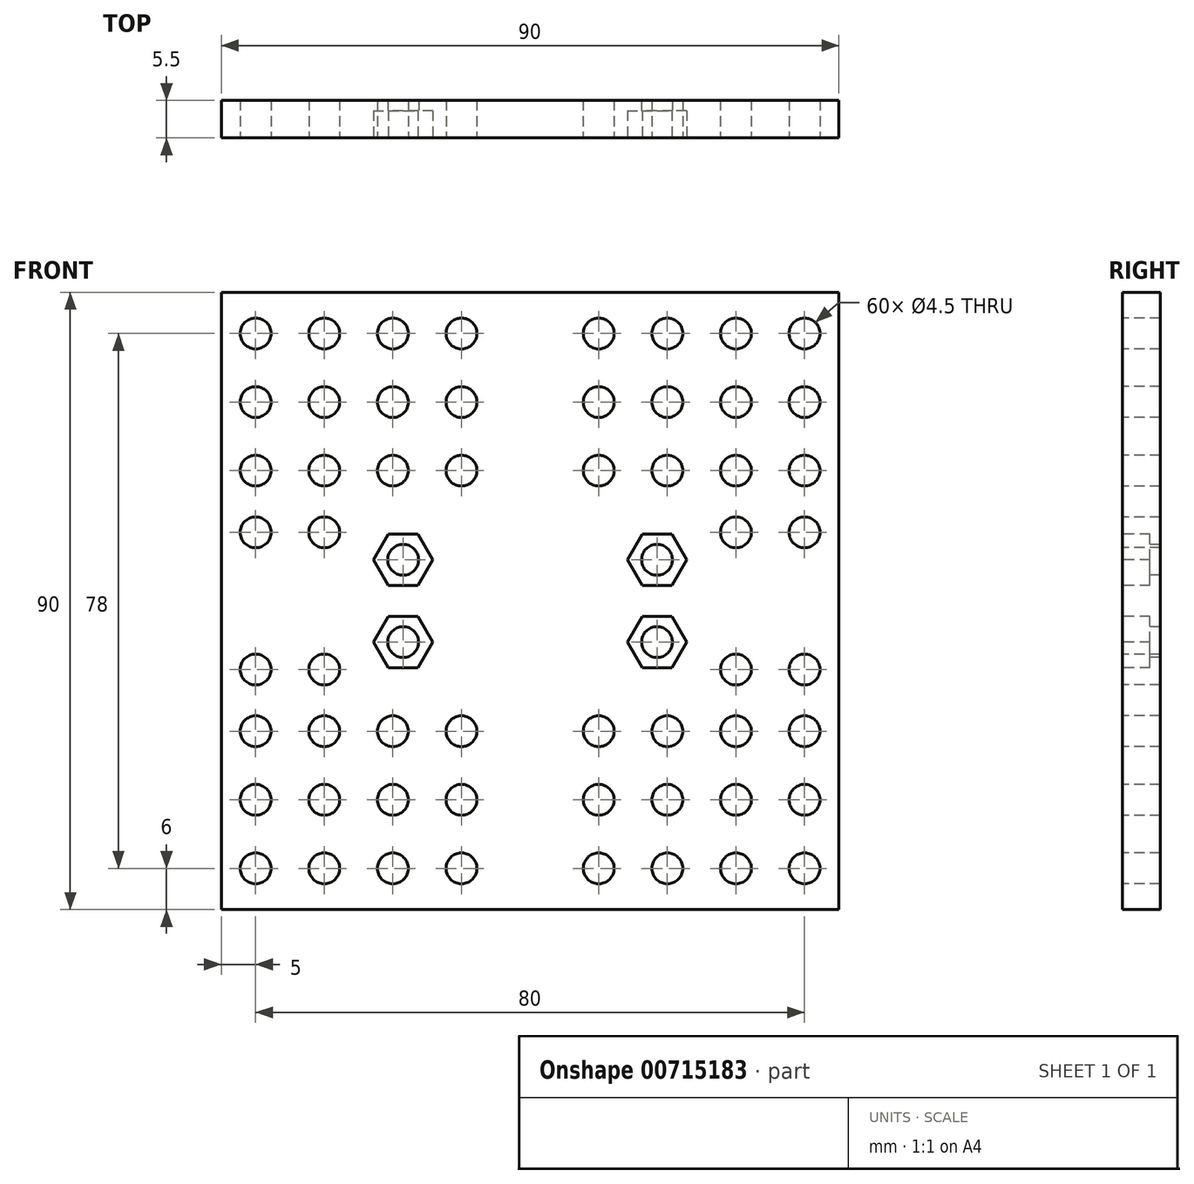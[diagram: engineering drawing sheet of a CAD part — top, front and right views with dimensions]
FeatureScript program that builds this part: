
annotation { "Feature Type Name" : "Feature", "Feature Type Description" : "" }
export const myFeature = defineFeature(function(context is Context, id is Id, definition is map)
    precondition{}
    {
        {
            var Q0;
            Q0=qCreatedBy(makeId("Front.planeOp"),FACE);
            var sketch = newSketch(context, id + "F0", { "sketchPlane" : qUnion([Q0])});
            skLineSegment(sketch, "E0.bottom", {"start": v(45, 45) * mm, "end": v(-45, 45) * mm});
            skLineSegment(sketch, "E0.top", {"start": v(45, -45) * mm, "end": v(-45, -45) * mm});
            skLineSegment(sketch, "E0.left", {"start": v(45, 45) * mm, "end": v(45, -45) * mm});
            skLineSegment(sketch, "E0.right", {"start": v(-45, 45) * mm, "end": v(-45, -45) * mm});
            skPoint(sketch, "E0.middle", {"position": v(0, 0) * mm});
            skSolve(sketch);
        }
        {
            var Q0;
            Q0 = qSketchRegion(id + "F0", true);
            extrude(context, id + "F1", {"entities" : qUnion([Q0]), "endBound" : BoundingType.SYMMETRIC, "oppositeDirection" : true, "depth" : 5.5 * mm, "offsetDistance" : 25 * mm});
        }
        {
            var Q0;
            Q0=makeQuery(id+"F1.opExtrude","CAP_FACE",FACE,{"disambiguationData":[OSD([sQuery(id+"F0.wireOp",EDGE,"E0.bottom"),sQuery(id+"F0.wireOp",EDGE,"E0.top"),sQuery(id+"F0.wireOp",EDGE,"E0.left"),sQuery(id+"F0.wireOp",EDGE,"E0.right")])],"isStart":true});
            var sketch = newSketch(context, id + "F2", { "sketchPlane" : qUnion([Q0])});
            skCircle(sketch, "E1.cCircle", {"center": v(-18.5, 6) * mm, "radius": 3.75 * mm, "construction": true});
            skLineSegment(sketch, "E1.0", {"start": v(-20.67, 9.75) * mm, "end": v(-16.33, 9.75) * mm});
            skLineSegment(sketch, "E1.1", {"start": v(-16.33, 9.75) * mm, "end": v(-14.17, 6) * mm});
            skLineSegment(sketch, "E1.2", {"start": v(-14.17, 6) * mm, "end": v(-16.33, 2.25) * mm});
            skLineSegment(sketch, "E1.3", {"start": v(-16.33, 2.25) * mm, "end": v(-20.67, 2.25) * mm});
            skLineSegment(sketch, "E1.4", {"start": v(-20.67, 2.25) * mm, "end": v(-22.83, 6) * mm});
            skLineSegment(sketch, "E1.5", {"start": v(-22.83, 6) * mm, "end": v(-20.67, 9.75) * mm});
            skPoint(sketch, "E1.0.midPoint", {"position": v(-18.5, 9.75) * mm});
            skCircle(sketch, "E2.cCircle", {"center": v(-18.5, -6) * mm, "radius": 3.75 * mm, "construction": true});
            skLineSegment(sketch, "E2.0", {"start": v(-20.67, -2.25) * mm, "end": v(-16.33, -2.25) * mm});
            skLineSegment(sketch, "E2.1", {"start": v(-16.33, -2.25) * mm, "end": v(-14.17, -6) * mm});
            skLineSegment(sketch, "E2.2", {"start": v(-14.17, -6) * mm, "end": v(-16.33, -9.75) * mm});
            skLineSegment(sketch, "E2.3", {"start": v(-16.33, -9.75) * mm, "end": v(-20.67, -9.75) * mm});
            skLineSegment(sketch, "E2.4", {"start": v(-20.67, -9.75) * mm, "end": v(-22.83, -6) * mm});
            skLineSegment(sketch, "E2.5", {"start": v(-22.83, -6) * mm, "end": v(-20.67, -2.25) * mm});
            skPoint(sketch, "E2.0.midPoint", {"position": v(-18.5, -2.25) * mm});
            skCircle(sketch, "E3.cCircle", {"center": v(18.5, -6) * mm, "radius": 3.75 * mm, "construction": true});
            skLineSegment(sketch, "E3.0", {"start": v(16.33, -2.25) * mm, "end": v(20.67, -2.25) * mm});
            skLineSegment(sketch, "E3.1", {"start": v(20.67, -2.25) * mm, "end": v(22.83, -6) * mm});
            skLineSegment(sketch, "E3.2", {"start": v(22.83, -6) * mm, "end": v(20.67, -9.75) * mm});
            skLineSegment(sketch, "E3.3", {"start": v(20.67, -9.75) * mm, "end": v(16.33, -9.75) * mm});
            skLineSegment(sketch, "E3.4", {"start": v(16.33, -9.75) * mm, "end": v(14.17, -6) * mm});
            skLineSegment(sketch, "E3.5", {"start": v(14.17, -6) * mm, "end": v(16.33, -2.25) * mm});
            skPoint(sketch, "E3.0.midPoint", {"position": v(18.5, -2.25) * mm});
            skCircle(sketch, "E4.cCircle", {"center": v(18.5, 6) * mm, "radius": 3.75 * mm, "construction": true});
            skLineSegment(sketch, "E4.0", {"start": v(20.67, 2.25) * mm, "end": v(16.33, 2.25) * mm});
            skLineSegment(sketch, "E4.1", {"start": v(16.33, 2.25) * mm, "end": v(14.17, 6) * mm});
            skLineSegment(sketch, "E4.2", {"start": v(14.17, 6) * mm, "end": v(16.33, 9.75) * mm});
            skLineSegment(sketch, "E4.3", {"start": v(16.33, 9.75) * mm, "end": v(20.67, 9.75) * mm});
            skLineSegment(sketch, "E4.4", {"start": v(20.67, 9.75) * mm, "end": v(22.83, 6) * mm});
            skLineSegment(sketch, "E4.5", {"start": v(22.83, 6) * mm, "end": v(20.67, 2.25) * mm});
            skPoint(sketch, "E4.0.midPoint", {"position": v(18.5, 2.25) * mm});
            skSolve(sketch);
        }
        {
            var Q0;
            Q0 = qSketchRegion(id + "F2", true);
            extrude(context, id + "F3", {"entities" : qUnion([Q0]), "operationType" : NewBodyOperationType.REMOVE, "oppositeDirection" : true, "depth" : 4 * mm, "offsetDistance" : 25 * mm});
        }
        {
            var Q0;
            Q0=makeQuery(id+"F1.opExtrude","CAP_FACE",FACE,{"disambiguationData":[OSD([sQuery(id+"F0.wireOp",EDGE,"E0.bottom"),sQuery(id+"F0.wireOp",EDGE,"E0.top"),sQuery(id+"F0.wireOp",EDGE,"E0.left"),sQuery(id+"F0.wireOp",EDGE,"E0.right")])],"isStart":true});
            var sketch = newSketch(context, id + "F4", { "sketchPlane" : qUnion([Q0])});
            skCircle(sketch, "E5", {"center": v(-18.5, 6) * mm, "radius": 2.25 * mm});
            skCircle(sketch, "E6", {"center": v(-18.5, -6) * mm, "radius": 2.25 * mm});
            skCircle(sketch, "E7", {"center": v(18.5, 6) * mm, "radius": 2.25 * mm});
            skCircle(sketch, "E8", {"center": v(18.5, -6) * mm, "radius": 2.25 * mm});
            skPoint(sketch, "E8.centerSnap0", {"position": v(18.5, -2.25) * mm});
            skSolve(sketch);
        }
        {
            var Q0;
            Q0 = qSketchRegion(id + "F4", true);
            extrude(context, id + "F5", {"entities" : qUnion([Q0]), "operationType" : NewBodyOperationType.REMOVE, "endBound" : BoundingType.THROUGH_ALL, "oppositeDirection" : true, "depth" : 25 * mm, "offsetDistance" : 25 * mm});
        }
        {
            var Q0;
            Q0=makeQuery(id+"F1.opExtrude","CAP_FACE",FACE,{"disambiguationData":[OSD([sQuery(id+"F0.wireOp",EDGE,"E0.bottom"),sQuery(id+"F0.wireOp",EDGE,"E0.top"),sQuery(id+"F0.wireOp",EDGE,"E0.left"),sQuery(id+"F0.wireOp",EDGE,"E0.right")])],"isStart":true});
            var sketch = newSketch(context, id + "F6", { "sketchPlane" : qUnion([Q0])});
            skLineSegment(sketch, "E9.bottom", {"start": v(24.5, 12.5) * mm, "end": v(-24.5, 12.5) * mm, "construction": true});
            skLineSegment(sketch, "E9.top", {"start": v(24.5, -12.5) * mm, "end": v(-24.5, -12.5) * mm, "construction": true});
            skLineSegment(sketch, "E9.left", {"start": v(24.5, 12.5) * mm, "end": v(24.5, -12.5) * mm, "construction": true});
            skLineSegment(sketch, "E9.right", {"start": v(-24.5, 12.5) * mm, "end": v(-24.5, -12.5) * mm, "construction": true});
            skPoint(sketch, "E9.middle", {"position": v(0, 0) * mm});
            skPoint(sketch, "E10", {"position": v(-40, 39) * mm});
            skCircle(sketch, "E11", {"center": v(-40, 39) * mm, "radius": 2.25 * mm, "construction": true});
            skCircle(sketch, "E12.1.0.0", {"center": v(-30, 39) * mm, "radius": 2.25 * mm, "construction": true});
            skCircle(sketch, "E12.2.0.0", {"center": v(-20, 39) * mm, "radius": 2.25 * mm, "construction": true});
            skCircle(sketch, "E12.3.0.0", {"center": v(-10, 39) * mm, "radius": 2.25 * mm, "construction": true});
            skCircle(sketch, "E12.4.0.0", {"center": v(0, 39) * mm, "radius": 2.25 * mm, "construction": true});
            skCircle(sketch, "E12.5.0.0", {"center": v(10, 39) * mm, "radius": 2.25 * mm, "construction": true});
            skCircle(sketch, "E12.6.0.0", {"center": v(20, 39) * mm, "radius": 2.25 * mm, "construction": true});
            skCircle(sketch, "E12.7.0.0", {"center": v(30, 39) * mm, "radius": 2.25 * mm, "construction": true});
            skCircle(sketch, "E12.8.0.0", {"center": v(40, 39) * mm, "radius": 2.25 * mm, "construction": true});
            skLineSegment(sketch, "E12.direction1", {"start": v(-40, 39) * mm, "end": v(-30, 39) * mm, "construction": true});
            skCircle(sketch, "E13.0.1.0", {"center": v(-30, 29) * mm, "radius": 2.25 * mm, "construction": true});
            skCircle(sketch, "E13.0.1.1", {"center": v(-10, 29) * mm, "radius": 2.25 * mm, "construction": true});
            skPoint(sketch, "E13.0.1.2", {"position": v(-40, 29) * mm});
            skLineSegment(sketch, "E13.0.1.3", {"start": v(-40, 29) * mm, "end": v(-30, 29) * mm, "construction": true});
            skCircle(sketch, "E13.0.1.4", {"center": v(40, 29) * mm, "radius": 2.25 * mm, "construction": true});
            skCircle(sketch, "E13.0.1.5", {"center": v(-20, 29) * mm, "radius": 2.25 * mm, "construction": true});
            skCircle(sketch, "E13.0.1.6", {"center": v(-40, 29) * mm, "radius": 2.25 * mm, "construction": true});
            skCircle(sketch, "E13.0.1.7", {"center": v(10, 29) * mm, "radius": 2.25 * mm, "construction": true});
            skCircle(sketch, "E13.0.1.8", {"center": v(20, 29) * mm, "radius": 2.25 * mm, "construction": true});
            skCircle(sketch, "E13.0.1.9", {"center": v(0, 29) * mm, "radius": 2.25 * mm, "construction": true});
            skCircle(sketch, "E13.0.1.10", {"center": v(30, 29) * mm, "radius": 2.25 * mm, "construction": true});
            skLineSegment(sketch, "E13.direction1", {"start": v(-40, 39) * mm, "end": v(-15, 39) * mm, "construction": true});
            skLineSegment(sketch, "E13.direction2", {"start": v(-40, 39) * mm, "end": v(-40, 29) * mm, "construction": true});
            skLineSegment(sketch, "E14", {"start": v(0, 0) * mm, "end": v(53, 0) * mm, "construction": true});
            skCircle(sketch, "E15.MirrorC", {"center": v(0, -39) * mm, "radius": 2.25 * mm, "construction": true});
            skLineSegment(sketch, "E16.MirrorCS", {"start": v(-40, -29) * mm, "end": v(-30, -29) * mm, "construction": true});
            skCircle(sketch, "E17.MirrorC", {"center": v(20, -39) * mm, "radius": 2.25 * mm, "construction": true});
            skCircle(sketch, "E18.MirrorC", {"center": v(30, -39) * mm, "radius": 2.25 * mm, "construction": true});
            skCircle(sketch, "E19.MirrorC", {"center": v(40, -39) * mm, "radius": 2.25 * mm, "construction": true});
            skCircle(sketch, "E20.MirrorC", {"center": v(40, -19) * mm, "radius": 2.25 * mm, "construction": true});
            skCircle(sketch, "E21.MirrorC", {"center": v(-40, -19) * mm, "radius": 2.25 * mm, "construction": true});
            skCircle(sketch, "E22.MirrorC", {"center": v(10, -29) * mm, "radius": 2.25 * mm, "construction": true});
            skPoint(sketch, "E23.MirrorP", {"position": v(-40, -39) * mm});
            skCircle(sketch, "E24.MirrorC", {"center": v(-30, -39) * mm, "radius": 2.25 * mm, "construction": true});
            skCircle(sketch, "E25.MirrorC", {"center": v(30, -29) * mm, "radius": 2.25 * mm, "construction": true});
            skCircle(sketch, "E26.MirrorC", {"center": v(30, -19) * mm, "radius": 2.25 * mm, "construction": true});
            skCircle(sketch, "E27.MirrorC", {"center": v(40, -29) * mm, "radius": 2.25 * mm, "construction": true});
            skCircle(sketch, "E28.MirrorC", {"center": v(-20, -19) * mm, "radius": 2.25 * mm, "construction": true});
            skPoint(sketch, "E29.MirrorP", {"position": v(-40, -29) * mm});
            skCircle(sketch, "E30.MirrorC", {"center": v(0, -19) * mm, "radius": 2.25 * mm, "construction": true});
            skCircle(sketch, "E31.MirrorC", {"center": v(10, -19) * mm, "radius": 2.25 * mm, "construction": true});
            skCircle(sketch, "E32.MirrorC", {"center": v(20, -29) * mm, "radius": 2.25 * mm, "construction": true});
            skLineSegment(sketch, "E33.MirrorCS", {"start": v(-40, -39) * mm, "end": v(-15, -39) * mm, "construction": true});
            skCircle(sketch, "E34.MirrorC", {"center": v(10, -39) * mm, "radius": 2.25 * mm, "construction": true});
            skLineSegment(sketch, "E35.MirrorCS", {"start": v(-40, -19) * mm, "end": v(-30, -19) * mm, "construction": true});
            skCircle(sketch, "E36.MirrorC", {"center": v(-30, -19) * mm, "radius": 2.25 * mm, "construction": true});
            skCircle(sketch, "E37.MirrorC", {"center": v(0, -29) * mm, "radius": 2.25 * mm, "construction": true});
            skCircle(sketch, "E38.MirrorC", {"center": v(20, -19) * mm, "radius": 2.25 * mm, "construction": true});
            skCircle(sketch, "E39.MirrorC", {"center": v(-30, -29) * mm, "radius": 2.25 * mm, "construction": true});
            skCircle(sketch, "E40.MirrorC", {"center": v(-10, -29) * mm, "radius": 2.25 * mm, "construction": true});
            skLineSegment(sketch, "E41.MirrorCS", {"start": v(-40, -39) * mm, "end": v(-40, -29) * mm, "construction": true});
            skLineSegment(sketch, "E42.MirrorCS", {"start": v(-40, -39) * mm, "end": v(-30, -39) * mm, "construction": true});
            skCircle(sketch, "E43.MirrorC", {"center": v(-20, -29) * mm, "radius": 2.25 * mm, "construction": true});
            skCircle(sketch, "E44.MirrorC", {"center": v(-10, -39) * mm, "radius": 2.25 * mm, "construction": true});
            skCircle(sketch, "E45.MirrorC", {"center": v(-40, -29) * mm, "radius": 2.25 * mm, "construction": true});
            skCircle(sketch, "E46.MirrorC", {"center": v(-10, -19) * mm, "radius": 2.25 * mm, "construction": true});
            skCircle(sketch, "E47.MirrorC", {"center": v(-40, -39) * mm, "radius": 2.25 * mm, "construction": true});
            skCircle(sketch, "E48.MirrorC", {"center": v(-20, -39) * mm, "radius": 2.25 * mm, "construction": true});
            skCircle(sketch, "E49", {"center": v(-40, 0) * mm, "radius": 2.25 * mm, "construction": true});
            skPoint(sketch, "E49.centerSnap0", {"position": v(-24.5, 0) * mm});
            skCircle(sketch, "E50", {"center": v(-30, 0) * mm, "radius": 2.25 * mm, "construction": true});
            skLineSegment(sketch, "E51", {"start": v(0, 0) * mm, "end": v(0, 9.62) * mm, "construction": true});
            skCircle(sketch, "E52.0.0.2", {"center": v(-30, 19) * mm, "radius": 2.25 * mm, "construction": true});
            skCircle(sketch, "E52.2.0.2", {"center": v(-10, 19) * mm, "radius": 2.25 * mm, "construction": true});
            skPoint(sketch, "E52.4.0.2", {"position": v(-40, 19) * mm});
            skLineSegment(sketch, "E52.5.0.2", {"start": v(-40, 19) * mm, "end": v(-30, 19) * mm, "construction": true});
            skCircle(sketch, "E52.8.0.2", {"center": v(40, 19) * mm, "radius": 2.25 * mm, "construction": true});
            skCircle(sketch, "E52.10.0.2", {"center": v(-20, 19) * mm, "radius": 2.25 * mm, "construction": true});
            skCircle(sketch, "E52.12.0.2", {"center": v(-40, 19) * mm, "radius": 2.25 * mm, "construction": true});
            skCircle(sketch, "E52.14.0.2", {"center": v(10, 19) * mm, "radius": 2.25 * mm, "construction": true});
            skCircle(sketch, "E52.16.0.2", {"center": v(20, 19) * mm, "radius": 2.25 * mm, "construction": true});
            skCircle(sketch, "E52.18.0.2", {"center": v(0, 19) * mm, "radius": 2.25 * mm, "construction": true});
            skCircle(sketch, "E52.20.0.2", {"center": v(30, 19) * mm, "radius": 2.25 * mm, "construction": true});
            skCircle(sketch, "E53.0.1.0", {"center": v(-40, 10) * mm, "radius": 2.25 * mm, "construction": true});
            skCircle(sketch, "E53.0.1.1", {"center": v(-30, 10) * mm, "radius": 2.25 * mm, "construction": true});
            skLineSegment(sketch, "E53.direction1", {"start": v(-40, 0) * mm, "end": v(-15, 0) * mm, "construction": true});
            skLineSegment(sketch, "E53.direction2", {"start": v(-40, 0) * mm, "end": v(-40, 10) * mm, "construction": true});
            skCircle(sketch, "E54.MirrorC", {"center": v(40, 0) * mm, "radius": 2.25 * mm, "construction": true});
            skLineSegment(sketch, "E55.MirrorCS", {"start": v(40, 0) * mm, "end": v(40, 10) * mm, "construction": true});
            skCircle(sketch, "E56.MirrorC", {"center": v(30, 10) * mm, "radius": 2.25 * mm, "construction": true});
            skCircle(sketch, "E57.MirrorC", {"center": v(30, 0) * mm, "radius": 2.25 * mm, "construction": true});
            skCircle(sketch, "E58.MirrorC", {"center": v(40, 10) * mm, "radius": 2.25 * mm, "construction": true});
            skCircle(sketch, "E59.MirrorC", {"center": v(-30, -10) * mm, "radius": 2.25 * mm, "construction": true});
            skCircle(sketch, "E60.MirrorC", {"center": v(-40, -10) * mm, "radius": 2.25 * mm, "construction": true});
            skCircle(sketch, "E61.MirrorC", {"center": v(30, -10) * mm, "radius": 2.25 * mm, "construction": true});
            skCircle(sketch, "E62.MirrorC", {"center": v(40, -10) * mm, "radius": 2.25 * mm, "construction": true});
            skSolve(sketch);
        }
        {
            var Q0;
            Q0=sQuery(id+"F6.wireOp",VERTEX,"E10");
            var Q1;
            Q1=sQuery(id+"F6.wireOp",VERTEX,"E12.1.0.0.center");
            var Q2;
            Q2=sQuery(id+"F6.wireOp",VERTEX,"E12.2.0.0.center");
            var Q3;
            Q3=sQuery(id+"F6.wireOp",VERTEX,"E12.3.0.0.center");
            var Q4;
            Q4=sQuery(id+"F6.wireOp",VERTEX,"E12.5.0.0.center");
            var Q5;
            Q5=sQuery(id+"F6.wireOp",VERTEX,"E12.6.0.0.center");
            var Q6;
            Q6=sQuery(id+"F6.wireOp",VERTEX,"E12.7.0.0.center");
            var Q7;
            Q7=sQuery(id+"F6.wireOp",VERTEX,"E12.8.0.0.center");
            var Q8;
            Q8=sQuery(id+"F6.wireOp",VERTEX,"E13.0.1.4.center");
            var Q9;
            Q9=sQuery(id+"F6.wireOp",VERTEX,"E13.0.1.10.center");
            var Q10;
            Q10=sQuery(id+"F6.wireOp",VERTEX,"E13.0.1.8.center");
            var Q11;
            Q11=sQuery(id+"F6.wireOp",VERTEX,"E13.0.1.1.center");
            var Q12;
            Q12=sQuery(id+"F6.wireOp",VERTEX,"E13.0.1.7.center");
            var Q13;
            Q13=sQuery(id+"F6.wireOp",VERTEX,"E13.0.1.0.center");
            var Q14;
            Q14=sQuery(id+"F6.wireOp",VERTEX,"E13.0.1.5.center");
            var Q15;
            Q15=sQuery(id+"F6.wireOp",VERTEX,"E13.0.1.2");
            var Q16;
            Q16=sQuery(id+"F6.wireOp",VERTEX,"E52.20.0.2.center");
            var Q17;
            Q17=sQuery(id+"F6.wireOp",VERTEX,"E52.5.0.2.start");
            var Q18;
            Q18=sQuery(id+"F6.wireOp",VERTEX,"E52.14.0.2.center");
            var Q19;
            Q19=sQuery(id+"F6.wireOp",VERTEX,"E52.2.0.2.center");
            var Q20;
            Q20=sQuery(id+"F6.wireOp",VERTEX,"E52.16.0.2.center");
            var Q21;
            Q21=sQuery(id+"F6.wireOp",VERTEX,"E52.10.0.2.center");
            var Q22;
            Q22=sQuery(id+"F6.wireOp",VERTEX,"E52.8.0.2.center");
            var Q23;
            Q23=sQuery(id+"F6.wireOp",VERTEX,"E52.5.0.2.end");
            var Q24;
            Q24=sQuery(id+"F6.wireOp",VERTEX,"E56.MirrorC.center");
            var Q25;
            Q25=sQuery(id+"F6.wireOp",VERTEX,"E61.MirrorC.center");
            var Q26;
            Q26=sQuery(id+"F6.wireOp",VERTEX,"E19.MirrorC.center");
            var Q27;
            Q27=sQuery(id+"F6.wireOp",VERTEX,"E55.MirrorCS.end");
            var Q28;
            Q28=sQuery(id+"F6.wireOp",VERTEX,"E25.MirrorC.center");
            var Q29;
            Q29=sQuery(id+"F6.wireOp",VERTEX,"E18.MirrorC.center");
            var Q30;
            Q30=sQuery(id+"F6.wireOp",VERTEX,"E20.MirrorC.center");
            var Q31;
            Q31=sQuery(id+"F6.wireOp",VERTEX,"E62.MirrorC.center");
            var Q32;
            Q32=sQuery(id+"F6.wireOp",VERTEX,"E26.MirrorC.center");
            var Q33;
            Q33=sQuery(id+"F6.wireOp",VERTEX,"E27.MirrorC.center");
            var Q34;
            Q34=sQuery(id+"F6.wireOp",VERTEX,"E59.MirrorC.center");
            var Q35;
            Q35=sQuery(id+"F6.wireOp",VERTEX,"E21.MirrorC.center");
            var Q36;
            Q36=sQuery(id+"F6.wireOp",VERTEX,"E29.MirrorP");
            var Q37;
            Q37=sQuery(id+"F6.wireOp",VERTEX,"E36.MirrorC.center");
            var Q38;
            Q38=sQuery(id+"F6.wireOp",VERTEX,"E42.MirrorCS.end");
            var Q39;
            Q39=sQuery(id+"F6.wireOp",VERTEX,"E53.0.1.1.center");
            var Q40;
            Q40=sQuery(id+"F6.wireOp",VERTEX,"E60.MirrorC.center");
            var Q41;
            Q41=sQuery(id+"F6.wireOp",VERTEX,"E33.MirrorCS.start");
            var Q42;
            Q42=sQuery(id+"F6.wireOp",VERTEX,"E53.0.1.0.center");
            var Q43;
            Q43=sQuery(id+"F6.wireOp",VERTEX,"E16.MirrorCS.end");
            var Q44;
            Q44=sQuery(id+"F6.wireOp",VERTEX,"E40.MirrorC.center");
            var Q45;
            Q45=sQuery(id+"F6.wireOp",VERTEX,"E17.MirrorC.center");
            var Q46;
            Q46=sQuery(id+"F6.wireOp",VERTEX,"E46.MirrorC.center");
            var Q47;
            Q47=sQuery(id+"F6.wireOp",VERTEX,"E32.MirrorC.center");
            var Q48;
            Q48=sQuery(id+"F6.wireOp",VERTEX,"E31.MirrorC.center");
            var Q49;
            Q49=sQuery(id+"F6.wireOp",VERTEX,"E22.MirrorC.center");
            var Q50;
            Q50=sQuery(id+"F6.wireOp",VERTEX,"E28.MirrorC.center");
            var Q51;
            Q51=sQuery(id+"F6.wireOp",VERTEX,"E48.MirrorC.center");
            var Q52;
            Q52=sQuery(id+"F6.wireOp",VERTEX,"E34.MirrorC.center");
            var Q53;
            Q53=sQuery(id+"F6.wireOp",VERTEX,"E44.MirrorC.center");
            var Q54;
            Q54=sQuery(id+"F6.wireOp",VERTEX,"E43.MirrorC.center");
            var Q55;
            Q55=sQuery(id+"F6.wireOp",VERTEX,"E38.MirrorC.center");
            var Q56;
            Q56=makeQuery(id+"F1.opExtrude","SWEPT_BODY",BODY,{"disambiguationData":[OSD([sQuery(id+"F0.wireOp",EDGE,"E0.bottom"),sQuery(id+"F0.wireOp",EDGE,"E0.top"),sQuery(id+"F0.wireOp",EDGE,"E0.left"),sQuery(id+"F0.wireOp",EDGE,"E0.right")])]});
            hole(context, id + "F7", {"style" : HoleStyle.SIMPLE, "endStyle" : HoleEndStyle.THROUGH, "holeDiameter" : 4.5 * mm, "majorDiameter" : 5 * mm, "isTappedThrough" : true, "tappedDepth" : 12 * mm, "tapClearance" : 3, "locations" : qUnion([Q0, Q1, Q2, Q3, Q4, Q5, Q6, Q7, Q8, Q9, Q10, Q11, Q12, Q13, Q14, Q15, Q16, Q17, Q18, Q19, Q20, Q21, Q22, Q23, Q24, Q25, Q26, Q27, Q28, Q29, Q30, Q31, Q32, Q33, Q34, Q35, Q36, Q37, Q38, Q39, Q40, Q41, Q42, Q43, Q44, Q45, Q46, Q47, Q48, Q49, Q50, Q51, Q52, Q53, Q54, Q55]), "scope" : qUnion([Q56])});
        }
    });
